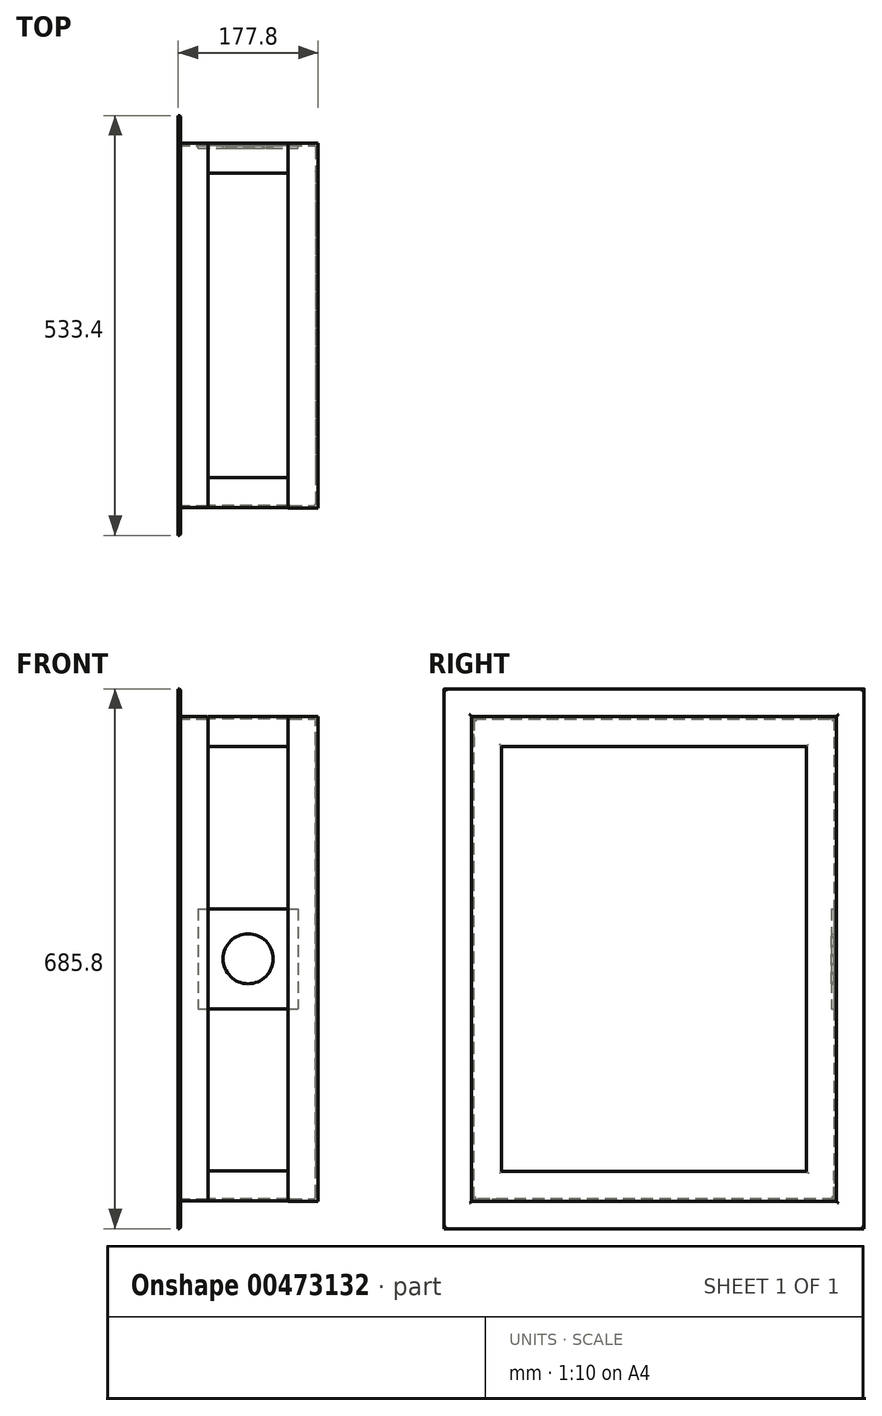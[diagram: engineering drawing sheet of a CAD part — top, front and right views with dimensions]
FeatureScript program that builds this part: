
annotation { "Feature Type Name" : "Feature", "Feature Type Description" : "" }
export const myFeature = defineFeature(function(context is Context, id is Id, definition is map)
    precondition{}
    {
        {
            var Q0;
            Q0=qCreatedBy(makeId("Right.planeOp"),FACE);
            var sketch = newSketch(context, id + "F0", { "sketchPlane" : qUnion([Q0])});
            skLineSegment(sketch, "E0.bottom", {"start": v(-228.6, 304.8) * mm, "end": v(228.6, 304.8) * mm});
            skLineSegment(sketch, "E0.top", {"start": v(-228.6, -304.8) * mm, "end": v(228.6, -304.8) * mm});
            skLineSegment(sketch, "E0.left", {"start": v(-228.6, 304.8) * mm, "end": v(-228.6, -304.8) * mm});
            skLineSegment(sketch, "E0.right", {"start": v(228.6, 304.8) * mm, "end": v(228.6, -304.8) * mm});
            skPoint(sketch, "E0.middle", {"position": v(0, 0) * mm});
            skSolve(sketch);
        }
        {
            var Q0;
            Q0=qCreatedBy(makeId("Front.planeOp"),FACE);
            var sketch = newSketch(context, id + "F1", { "sketchPlane" : qUnion([Q0])});
            skLineSegment(sketch, "E1.0", {"start": v(0, 304.8) * mm, "end": v(0, -304.8) * mm, "construction": true});
            skLineSegment(sketch, "E2.bottom", {"start": v(0, -304.8) * mm, "end": v(38.1, -304.8) * mm});
            skLineSegment(sketch, "E2.top", {"start": v(0, -342.9) * mm, "end": v(0.5, -342.9) * mm});
            skLineSegment(sketch, "E2.left", {"start": v(0, -304.8) * mm, "end": v(0, -342.9) * mm});
            skLineSegment(sketch, "E2.right", {"start": v(38.1, -304.8) * mm, "end": v(38.1, -305.3) * mm});
            skLineSegment(sketch, "E3.top", {"start": v(35.56, -307.85) * mm, "end": v(5.59, -307.85) * mm});
            skLineSegment(sketch, "E3.right", {"start": v(3.05, -340.36) * mm, "end": v(3.05, -310.39) * mm});
            skPoint(sketch, "E4.visualSharp", {"position": v(3.05, -342.9) * mm});
            skArc(sketch, "E4.filletArc", {"start": v(0.5, -342.9) * mm, "mid": v(2.3, -342.16) * mm, "end": v(3.05, -340.36) * mm});
            skPoint(sketch, "E5.visualSharp", {"position": v(38.1, -307.85) * mm});
            skArc(sketch, "E5.filletArc", {"start": v(35.56, -307.85) * mm, "mid": v(37.36, -307.1) * mm, "end": v(38.1, -305.3) * mm});
            skPoint(sketch, "E6.visualSharp", {"position": v(3.05, -307.85) * mm});
            skArc(sketch, "E6.filletArc", {"start": v(5.59, -307.85) * mm, "mid": v(3.8, -308.6) * mm, "end": v(3.05, -310.39) * mm});
            skSolve(sketch);
        }
        {
            var Q0;
            Q0 = qSketchRegion(id + "F1", true);
            var Q1;
            Q1 = qConstructionFilter(qBodyType(qCreatedBy(id + "F0" ,EDGE), BodyType.WIRE), ConstructionObject.NO);
            sweep(context, id + "F2", {"profiles" : qUnion([Q0]), "path" : qUnion([Q1])});
        }
        {
            var Q0;
            Q0=qCreatedBy(makeId("Right.planeOp"),FACE);
            cPlane(context, id + "F3", {"entities" : qUnion([Q0]), "cplaneType" : CPlaneType.OFFSET, "offset" : 177.8 * mm, "width" : 152.4 * mm, "height" : 152.4 * mm});
        }
        {
            var Q0;
            Q0=qCreatedBy(id+"F3.planeOp",FACE);
            var sketch = newSketch(context, id + "F4", { "sketchPlane" : qUnion([Q0])});
            skLineSegment(sketch, "E7.0", {"start": v(231.78, 307.98) * mm, "end": v(231.78, -307.98) * mm});
            skLineSegment(sketch, "E8.0", {"start": v(231.78, -307.98) * mm, "end": v(-231.77, -307.98) * mm});
            skLineSegment(sketch, "E9.0", {"start": v(-231.78, -307.98) * mm, "end": v(-231.78, 307.98) * mm});
            skLineSegment(sketch, "E10.0", {"start": v(-231.78, 307.98) * mm, "end": v(231.78, 307.98) * mm});
            skLineSegment(sketch, "E11.0", {"start": v(0, 304.8) * mm, "end": v(0, -304.8) * mm, "construction": true});
            skLineSegment(sketch, "E12", {"start": v(-279.78, 0) * mm, "end": v(421.02, 0) * mm, "construction": true});
            skPoint(sketch, "E12.startSnap0", {"position": v(-231.78, 0) * mm});
            skPoint(sketch, "E12.endSnap0", {"position": v(-231.78, 0) * mm});
            skPoint(sketch, "E13.orphan", {"position": v(-231.78, 304.8) * mm});
            skPoint(sketch, "E14.orphan", {"position": v(-231.78, -304.8) * mm});
            skSolve(sketch);
        }
        {
            var Q0;
            Q0=qCreatedBy(makeId("Front.planeOp"),FACE);
            var sketch = newSketch(context, id + "F5", { "sketchPlane" : qUnion([Q0])});
            skLineSegment(sketch, "E15.bottom", {"start": v(177.8, -307.98) * mm, "end": v(139.7, -307.98) * mm});
            skLineSegment(sketch, "E15.top", {"start": v(177.8, -269.88) * mm, "end": v(177.17, -269.88) * mm});
            skLineSegment(sketch, "E15.left", {"start": v(177.8, -307.98) * mm, "end": v(177.8, -269.88) * mm});
            skLineSegment(sketch, "E15.right", {"start": v(139.7, -307.98) * mm, "end": v(139.7, -307.34) * mm});
            skLineSegment(sketch, "E16.0", {"start": v(172.08, -304.8) * mm, "end": v(142.24, -304.8) * mm});
            skLineSegment(sketch, "E17.0", {"start": v(174.62, -302.26) * mm, "end": v(174.62, -272.42) * mm});
            skPoint(sketch, "E18.visualSharp", {"position": v(139.7, -304.8) * mm});
            skArc(sketch, "E18.filletArc", {"start": v(142.24, -304.8) * mm, "mid": v(140.44, -305.54) * mm, "end": v(139.7, -307.34) * mm});
            skArc(sketch, "E19.filletArc", {"start": v(172.08, -304.8) * mm, "mid": v(173.88, -304.06) * mm, "end": v(174.62, -302.26) * mm});
            skPoint(sketch, "E20.visualSharp", {"position": v(174.62, -269.88) * mm});
            skArc(sketch, "E20.filletArc", {"start": v(177.17, -269.88) * mm, "mid": v(175.37, -270.62) * mm, "end": v(174.63, -272.42) * mm});
            skSolve(sketch);
        }
        {
            var Q0;
            Q0 = qSketchRegion(id + "F5", true);
            var Q1;
            Q1 = qConstructionFilter(qBodyType(qCreatedBy(id + "F4" ,EDGE), BodyType.WIRE), ConstructionObject.NO);
            sweep(context, id + "F6", {"profiles" : qUnion([Q0]), "path" : qUnion([Q1])});
        }
        {
            var Q0;
            Q0=qCreatedBy(makeId("Right.planeOp"),FACE);
            cPlane(context, id + "F7", {"entities" : qUnion([Q0]), "cplaneType" : CPlaneType.OFFSET, "offset" : 38.1 * mm, "width" : 152.4 * mm, "height" : 152.4 * mm});
        }
        {
            var Q0;
            Q0=qCreatedBy(id+"F7.planeOp",FACE);
            var sketch = newSketch(context, id + "F8", { "sketchPlane" : qUnion([Q0])});
            skLineSegment(sketch, "E21.0.0", {"start": v(-228.6, -304.8) * mm, "end": v(-228.6, -269.75) * mm});
            skLineSegment(sketch, "E21.0.2", {"start": v(-228.6, 304.8) * mm, "end": v(-228.6, 269.75) * mm});
            skLineSegment(sketch, "E22.0.1", {"start": v(228.6, -304.8) * mm, "end": v(193.55, -304.8) * mm});
            skLineSegment(sketch, "E22.0.3", {"start": v(-228.6, -304.8) * mm, "end": v(-193.55, -304.8) * mm});
            skLineSegment(sketch, "E23.0.0", {"start": v(228.6, 304.8) * mm, "end": v(228.6, 269.75) * mm});
            skLineSegment(sketch, "E23.0.2", {"start": v(228.6, -304.8) * mm, "end": v(228.6, -269.75) * mm});
            skLineSegment(sketch, "E24.0.0", {"start": v(-228.6, 304.8) * mm, "end": v(-193.55, 304.8) * mm});
            skLineSegment(sketch, "E24.0.2", {"start": v(228.6, 304.8) * mm, "end": v(193.55, 304.8) * mm});
            skLineSegment(sketch, "E25.0.1", {"start": v(231.65, -307.85) * mm, "end": v(193.55, -307.85) * mm});
            skLineSegment(sketch, "E25.0.3", {"start": v(-231.65, -307.85) * mm, "end": v(-193.55, -307.85) * mm});
            skLineSegment(sketch, "E26.0.0", {"start": v(-231.65, -307.85) * mm, "end": v(-231.65, -269.75) * mm});
            skLineSegment(sketch, "E26.0.2", {"start": v(-231.65, 307.85) * mm, "end": v(-231.65, 269.75) * mm});
            skLineSegment(sketch, "E27.0.0", {"start": v(-231.65, 307.85) * mm, "end": v(-193.55, 307.85) * mm});
            skLineSegment(sketch, "E27.0.2", {"start": v(231.65, 307.85) * mm, "end": v(193.55, 307.85) * mm});
            skLineSegment(sketch, "E28.0.2", {"start": v(231.65, -307.85) * mm, "end": v(231.65, -269.75) * mm});
            skLineSegment(sketch, "E29.0", {"start": v(-231.65, -269.75) * mm, "end": v(-228.6, -269.75) * mm});
            skLineSegment(sketch, "E30.0", {"start": v(-193.55, 307.85) * mm, "end": v(-193.55, 304.8) * mm});
            skLineSegment(sketch, "E31", {"start": v(0, 428.44) * mm, "end": v(0, -639.54) * mm, "construction": true});
            skLineSegment(sketch, "E32", {"start": v(-457.97, 0) * mm, "end": v(369.53, 0) * mm, "construction": true});
            skLineSegment(sketch, "E33.MirrorCS", {"start": v(193.55, 307.85) * mm, "end": v(193.55, 304.8) * mm});
            skLineSegment(sketch, "E34.MirrorCS", {"start": v(-231.65, 269.75) * mm, "end": v(-228.6, 269.75) * mm});
            skLineSegment(sketch, "E35.trimOffspring", {"start": v(-231.65, -269.75) * mm, "end": v(-231.65, -307.85) * mm});
            skLineSegment(sketch, "E36.trimOffspring", {"start": v(-228.6, -269.75) * mm, "end": v(-228.6, -304.8) * mm});
            skLineSegment(sketch, "E37.trimOffspring", {"start": v(-193.55, -304.8) * mm, "end": v(-193.55, -307.85) * mm});
            skLineSegment(sketch, "E38.trimOffspring", {"start": v(-228.6, 269.75) * mm, "end": v(-228.6, 304.8) * mm});
            skLineSegment(sketch, "E39.trimOffspring", {"start": v(-231.65, 269.75) * mm, "end": v(-231.65, 307.85) * mm});
            skLineSegment(sketch, "E40.trimOffspring", {"start": v(193.55, -304.8) * mm, "end": v(193.55, -307.85) * mm});
            skLineSegment(sketch, "E41.trimOffspring", {"start": v(228.6, 269.75) * mm, "end": v(228.6, 304.8) * mm});
            skLineSegment(sketch, "E42.trimOffspring", {"start": v(231.65, 269.75) * mm, "end": v(231.65, 307.85) * mm});
            skLineSegment(sketch, "E43.trimOffspring", {"start": v(228.6, -269.75) * mm, "end": v(228.6, -304.8) * mm});
            skLineSegment(sketch, "E44.trimOffspring", {"start": v(231.65, -269.75) * mm, "end": v(231.65, -307.85) * mm});
            skLineSegment(sketch, "E45.trimOffspring", {"start": v(-193.55, 307.85) * mm, "end": v(-231.65, 307.85) * mm});
            skLineSegment(sketch, "E46.trimOffspring", {"start": v(193.55, 307.85) * mm, "end": v(231.65, 307.85) * mm});
            skLineSegment(sketch, "E47.trimOffspring", {"start": v(-193.55, 304.8) * mm, "end": v(-228.6, 304.8) * mm});
            skLineSegment(sketch, "E48.trimOffspring", {"start": v(193.55, 304.8) * mm, "end": v(228.6, 304.8) * mm});
            skLineSegment(sketch, "E49.trimOffspring", {"start": v(228.6, 269.75) * mm, "end": v(231.65, 269.75) * mm});
            skLineSegment(sketch, "E50.trimOffspring", {"start": v(228.6, -269.75) * mm, "end": v(231.65, -269.75) * mm});
            skLineSegment(sketch, "E51.trimOffspring", {"start": v(193.55, -304.8) * mm, "end": v(228.6, -304.8) * mm});
            skLineSegment(sketch, "E52.trimOffspring", {"start": v(193.55, -307.85) * mm, "end": v(231.65, -307.85) * mm});
            skLineSegment(sketch, "E53.trimOffspring", {"start": v(-193.55, -307.85) * mm, "end": v(-231.65, -307.85) * mm});
            skLineSegment(sketch, "E54.trimOffspring", {"start": v(-193.55, -304.8) * mm, "end": v(-228.6, -304.8) * mm});
            skSolve(sketch);
        }
        {
            var Q0;
            Q0 = qSketchRegion(id + "F8", true);
            extrude(context, id + "F9", {"entities" : qUnion([Q0]), "depth" : 101.6 * mm});
        }
        {
            var Q0;
            Q0=makeQuery(id+"F2.opSweep","SWEPT_FACE",FACE,{"disambiguationData":[OSD([sQuery(id+"F0.wireOp",EDGE,"E0.right"),sQuery(id+"F1.wireOp",EDGE,"E2.bottom")])]});
            var sketch = newSketch(context, id + "F10", { "sketchPlane" : qUnion([Q0])});
            skLineSegment(sketch, "E55", {"start": v(38.1, 0) * mm, "end": v(139.7, 0) * mm, "construction": true});
            skLineSegment(sketch, "E56.0", {"start": v(38.1, 304.8) * mm, "end": v(38.1, -304.8) * mm, "construction": true});
            skLineSegment(sketch, "E57.0", {"start": v(139.7, -307.34) * mm, "end": v(139.7, 307.34) * mm, "construction": true});
            skPoint(sketch, "E58.orphan", {"position": v(-118.15, 0) * mm});
            skLineSegment(sketch, "E59.bottom", {"start": v(25.4, 63.5) * mm, "end": v(152.4, 63.5) * mm});
            skLineSegment(sketch, "E59.top", {"start": v(25.4, -63.5) * mm, "end": v(152.4, -63.5) * mm});
            skLineSegment(sketch, "E59.left", {"start": v(25.4, 63.5) * mm, "end": v(25.4, -63.5) * mm});
            skLineSegment(sketch, "E59.right", {"start": v(152.4, 63.5) * mm, "end": v(152.4, -63.5) * mm});
            skPoint(sketch, "E59.middle", {"position": v(88.9, 0) * mm});
            skCircle(sketch, "E60", {"center": v(88.9, 0) * mm, "radius": 31.75 * mm});
            skSolve(sketch);
        }
        {
            var Q0;
            {var subQ0=sQuery(id+"F10.wireOp",EDGE,"E59.right");Q0=makeQuery(id+"F10.imprint","IMPRINT",FACE,{"disambiguationData":[TD([[makeQuery(id+"F10.imprint","IMPRINT",EDGE,{"derivedFrom":subQ0}),-1.0]])]});}
            var Q1;
            {var subQ0=sQuery(id+"F10.wireOp",EDGE,"E59.left");Q1=makeQuery(id+"F10.imprint","IMPRINT",FACE,{"disambiguationData":[TD([[makeQuery(id+"F10.imprint","IMPRINT",EDGE,{"derivedFrom":subQ0}),1.0]])]});}
            extrude(context, id + "F11", {"entities" : qUnion([Q0, Q1]), "depth" : 3.17 * mm});
        }
    });
